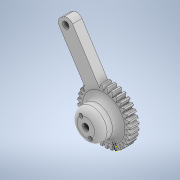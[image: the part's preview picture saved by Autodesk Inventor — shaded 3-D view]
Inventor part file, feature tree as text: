
AUTODESK INVENTOR PART (.ipt)
format: ipt  version: 2022 (Build 260153000, 153)  size: 1,224,192 bytes
history: native  units: in
note: dims shown in document units (in); Inventor stores cm internally (conversion verified against a paired STEP export)
features: sketch x8, extrude x6, projected_geometry x4, fillet x2, pattern_circular x1
ambient origin geometry x8: Origin, YZ Plane, XZ Plane, XY Plane, X Axis, Y Axis, Z Axis, Center Point
bodies: Solid1 (feature_tree)
feature tree (21):
  sketch  "Sketch1"  dims[d0=1.0in d1=1.0in d2=0.0in]
  extrude  "Extrusion1"  Depth=1.0in TaperAngle=0.0deg
  extrude  "Extrusion13"  Depth=0.13in
  extrude  "Extrusion14"  Depth=1.55in
  fillet  "Fillet1"  Radius=1.0in
  extrude  "Extrusion15"  Depth=0.125in
  extrude  "Extrusion16"  Depth=0.0787in
  sketch  "Sketch18"  dims[d51=1.0in d52=0.0in]
  extrude  "Extrusion17"  Depth=1.0in TaperAngle=0.0deg
  fillet  "Fillet2"  Radius=0.13in
  sketch  "Sketch2"  dims[d3=0.8in d37=0.13in]
  sketch  "Sketch14"  dims[d38=1.0in d39=0.0in d40=1.55in d41=1.0in d42=0.0in]
  projected_geometry  "Projected Loop3"
  sketch  "Sketch15"  dims[d43=0.125in d44=0.1772in]
  projected_geometry  "Projected Loop4"
  sketch  "Sketch16"  dims[d45=0.3543in d46=0.0787in]
  sketch  "Sketch17"  dims[d47=0.0787in d48=1.0in d49=0.0in d50=0.13in]
  projected_geometry  "Projected Loop5"
  sketch  "Sketch19"  dims[d53=0.6in d54=0.358in d55=0.0in d56=0.125in]
  projected_geometry  "Projected Loop6"
  pattern_circular  "CirPattern1"
